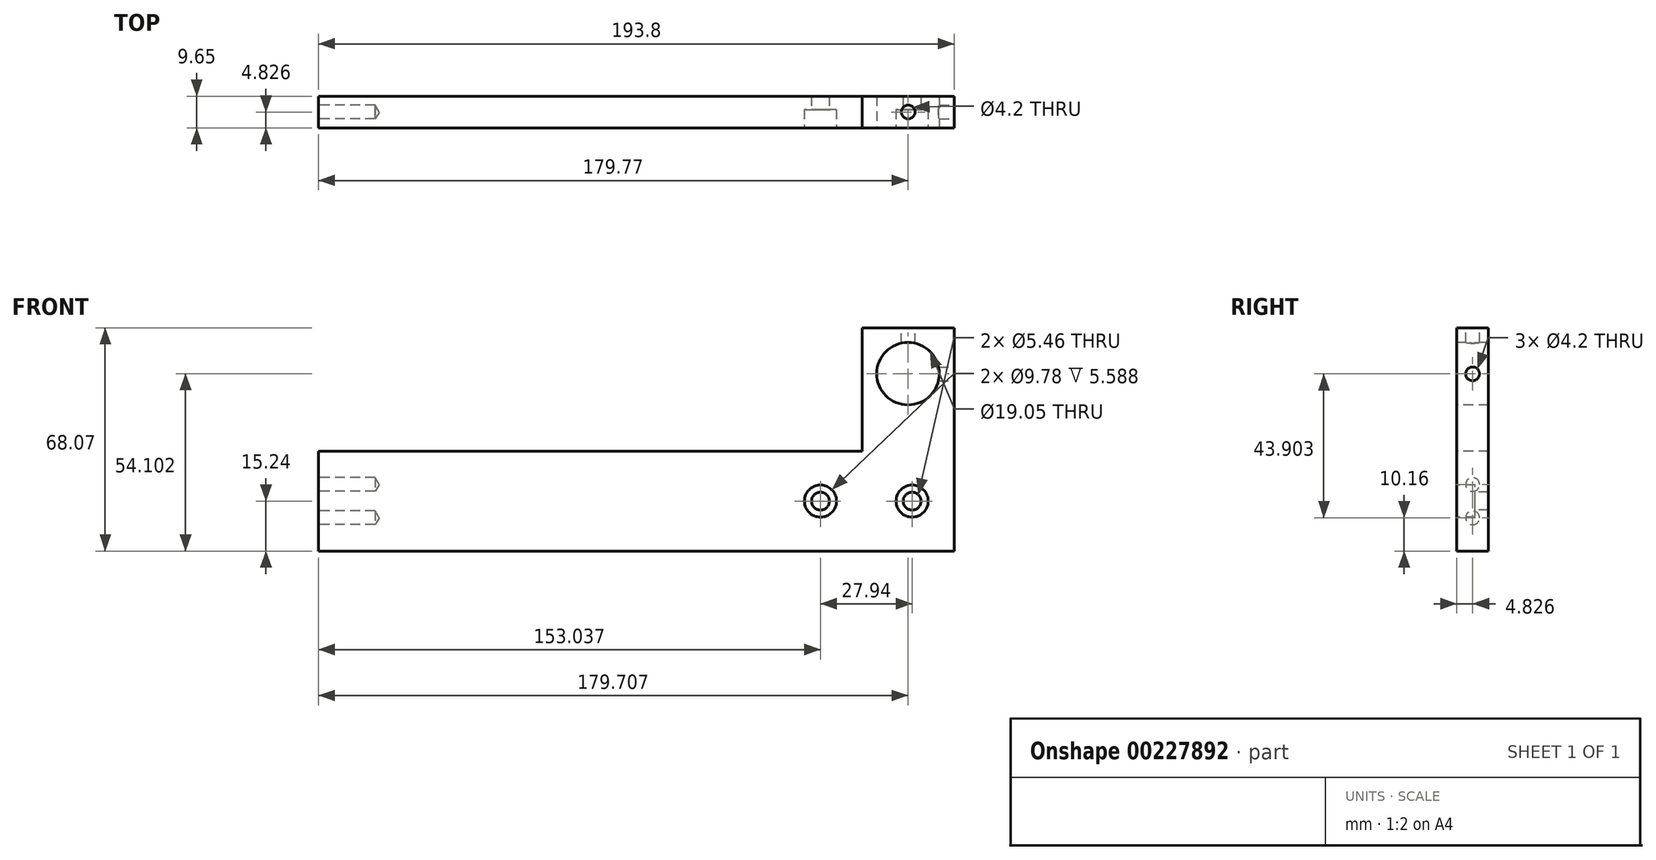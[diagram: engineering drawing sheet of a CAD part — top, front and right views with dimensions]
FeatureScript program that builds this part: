
annotation { "Feature Type Name" : "Feature", "Feature Type Description" : "" }
export const myFeature = defineFeature(function(context is Context, id is Id, definition is map)
    precondition{}
    {
        {
            var Q0;
            Q0=qCreatedBy(makeId("Front.planeOp"),FACE);
            var sketch = newSketch(context, id + "F0", { "sketchPlane" : qUnion([Q0])});
            skLineSegment(sketch, "E0", {"start": v(-79.83, 0) * mm, "end": v(113.97, 0) * mm});
            skLineSegment(sketch, "E1", {"start": v(-79.83, 0) * mm, "end": v(-79.83, 30.48) * mm});
            skLineSegment(sketch, "E2", {"start": v(-79.83, 30.48) * mm, "end": v(85.9, 30.48) * mm});
            skLineSegment(sketch, "E3", {"start": v(113.97, 0) * mm, "end": v(113.97, 68.07) * mm});
            skLineSegment(sketch, "E4", {"start": v(113.97, 68.07) * mm, "end": v(85.9, 68.07) * mm});
            skLineSegment(sketch, "E5", {"start": v(85.9, 68.07) * mm, "end": v(85.9, 30.48) * mm});
            skSolve(sketch);
        }
        {
            var Q0;
            Q0 = qSketchRegion(id + "F0", true);
            extrude(context, id + "F1", {"entities" : qUnion([Q0]), "oppositeDirection" : true, "depth" : 9.65 * mm});
        }
        {
            var Q0;
            Q0=makeQuery(id+"F1.opExtrude","CAP_FACE",FACE,{"disambiguationData":[OSD([sQuery(id+"F0.wireOp",EDGE,"E0"),sQuery(id+"F0.wireOp",EDGE,"E1"),sQuery(id+"F0.wireOp",EDGE,"E2"),sQuery(id+"F0.wireOp",EDGE,"E3"),sQuery(id+"F0.wireOp",EDGE,"E4"),sQuery(id+"F0.wireOp",EDGE,"E5")])],"isStart":true});
            var sketch = newSketch(context, id + "F2", { "sketchPlane" : qUnion([Q0])});
            skPoint(sketch, "E6", {"position": v(73.2, 15.24) * mm});
            skPoint(sketch, "E7", {"position": v(101.15, 15.24) * mm});
            skSolve(sketch);
        }
        {
            var Q0;
            Q0=sQuery(id+"F2.wireOp",VERTEX,"E6");
            var Q1;
            Q1=sQuery(id+"F2.wireOp",VERTEX,"E7");
            var Q2;
            Q2=makeQuery(id+"F1.opExtrude","SWEPT_BODY",BODY,{"disambiguationData":[OSD([sQuery(id+"F0.wireOp",EDGE,"E0"),sQuery(id+"F0.wireOp",EDGE,"E1"),sQuery(id+"F0.wireOp",EDGE,"E2"),sQuery(id+"F0.wireOp",EDGE,"E3"),sQuery(id+"F0.wireOp",EDGE,"E4"),sQuery(id+"F0.wireOp",EDGE,"E5")])]});
            hole(context, id + "F3", {"style" : HoleStyle.C_BORE, "endStyle" : HoleEndStyle.THROUGH, "holeDiameter" : 5.46 * mm, "cBoreDiameter" : 9.78 * mm, "cBoreDepth" : 5.6 * mm, "locations" : qUnion([Q0, Q1]), "scope" : qUnion([Q2]), "isTappedThrough" : true});
        }
        {
            var Q0;
            Q0=makeQuery(id+"F1.opExtrude","CAP_FACE",FACE,{"disambiguationData":[OSD([sQuery(id+"F0.wireOp",EDGE,"E0"),sQuery(id+"F0.wireOp",EDGE,"E1"),sQuery(id+"F0.wireOp",EDGE,"E2"),sQuery(id+"F0.wireOp",EDGE,"E3"),sQuery(id+"F0.wireOp",EDGE,"E4"),sQuery(id+"F0.wireOp",EDGE,"E5")])],"isStart":true});
            var sketch = newSketch(context, id + "F4", { "sketchPlane" : qUnion([Q0])});
            skPoint(sketch, "E8", {"position": v(99.88, 54.1) * mm});
            skSolve(sketch);
        }
        {
            var Q0;
            Q0=sQuery(id+"F4.wireOp",VERTEX,"E8");
            var Q1;
            Q1=makeQuery(id+"F1.opExtrude","SWEPT_BODY",BODY,{"disambiguationData":[OSD([sQuery(id+"F0.wireOp",EDGE,"E0"),sQuery(id+"F0.wireOp",EDGE,"E1"),sQuery(id+"F0.wireOp",EDGE,"E2"),sQuery(id+"F0.wireOp",EDGE,"E3"),sQuery(id+"F0.wireOp",EDGE,"E4"),sQuery(id+"F0.wireOp",EDGE,"E5")])]});
            hole(context, id + "F5", {"style" : HoleStyle.SIMPLE, "endStyle" : HoleEndStyle.THROUGH, "holeDiameter" : 19.05 * mm, "locations" : qUnion([Q0]), "scope" : qUnion([Q1]), "isTappedThrough" : true});
        }
        {
            var Q0;
            Q0=makeQuery(id+"F1.opExtrude","SWEPT_FACE",FACE,{"disambiguationData":[OSD([sQuery(id+"F0.wireOp",EDGE,"E4")])]});
            var sketch = newSketch(context, id + "F6", { "sketchPlane" : qUnion([Q0])});
            skPoint(sketch, "E9", {"position": v(99.94, 4.83) * mm});
            skSolve(sketch);
        }
        {
            var Q0;
            Q0=sQuery(id+"F6.wireOp",VERTEX,"E9");
            var Q1;
            Q1=makeQuery(id+"F1.opExtrude","SWEPT_BODY",BODY,{"disambiguationData":[OSD([sQuery(id+"F0.wireOp",EDGE,"E0"),sQuery(id+"F0.wireOp",EDGE,"E1"),sQuery(id+"F0.wireOp",EDGE,"E2"),sQuery(id+"F0.wireOp",EDGE,"E3"),sQuery(id+"F0.wireOp",EDGE,"E4"),sQuery(id+"F0.wireOp",EDGE,"E5")])]});
            hole(context, id + "F7", {"style" : HoleStyle.SIMPLE, "endStyle" : HoleEndStyle.BLIND, "standardTappedOrClearance" : lookupTablePath({ "standard" : "ISO", "engagement" : "75%", "pitch" : "0.8 mm", "size" : "M5", "type" : "Tapped" }), "standardBlindInLast" : lookupTablePath({ "standard" : "ISO", "engagement" : "75%", "pitch" : "0.8 mm", "size" : "M5", "type" : "Tapped" }), "holeDiameter" : 4.2 * mm, "holeDepth" : 12.7 * mm, "locations" : qUnion([Q0]), "scope" : qUnion([Q1]), "majorDiameter" : 5 * mm});
        }
        {
            var Q0;
            Q0=makeQuery(id+"F1.opExtrude","SWEPT_FACE",FACE,{"disambiguationData":[OSD([sQuery(id+"F0.wireOp",EDGE,"E3")])]});
            var sketch = newSketch(context, id + "F8", { "sketchPlane" : qUnion([Q0])});
            skPoint(sketch, "E10", {"position": v(4.83, 54.06) * mm});
            skPoint(sketch, "E11", {"position": v(0, 54.06) * mm});
            skSolve(sketch);
        }
        {
            var Q0;
            Q0=sQuery(id+"F8.wireOp",VERTEX,"E10");
            var Q1;
            Q1=makeQuery(id+"F1.opExtrude","SWEPT_BODY",BODY,{"disambiguationData":[OSD([sQuery(id+"F0.wireOp",EDGE,"E0"),sQuery(id+"F0.wireOp",EDGE,"E1"),sQuery(id+"F0.wireOp",EDGE,"E2"),sQuery(id+"F0.wireOp",EDGE,"E3"),sQuery(id+"F0.wireOp",EDGE,"E4"),sQuery(id+"F0.wireOp",EDGE,"E5")])]});
            hole(context, id + "F9", {"style" : HoleStyle.SIMPLE, "endStyle" : HoleEndStyle.BLIND, "standardTappedOrClearance" : lookupTablePath({ "standard" : "ISO", "engagement" : "75%", "pitch" : "0.8 mm", "size" : "M5", "type" : "Tapped" }), "standardBlindInLast" : lookupTablePath({ "standard" : "ISO", "engagement" : "75%", "pitch" : "0.8 mm", "size" : "M5", "type" : "Tapped" }), "holeDiameter" : 4.2 * mm, "holeDepth" : 12.7 * mm, "locations" : qUnion([Q0]), "scope" : qUnion([Q1]), "majorDiameter" : 5 * mm});
        }
        {
            var Q0;
            Q0=makeQuery(id+"F1.opExtrude","SWEPT_FACE",FACE,{"disambiguationData":[OSD([sQuery(id+"F0.wireOp",EDGE,"E1")])]});
            var sketch = newSketch(context, id + "F10", { "sketchPlane" : qUnion([Q0])});
            skPoint(sketch, "E12", {"position": v(-4.83, 64.78) * mm});
            skPoint(sketch, "E13", {"position": v(-4.83, 10.16) * mm});
            skPoint(sketch, "E14", {"position": v(-4.83, 20.32) * mm});
            skSolve(sketch);
        }
        {
            var Q0;
            Q0=sQuery(id+"F10.wireOp",VERTEX,"E14");
            var Q1;
            Q1=sQuery(id+"F10.wireOp",VERTEX,"E13");
            var Q2;
            Q2=makeQuery(id+"F1.opExtrude","SWEPT_BODY",BODY,{"disambiguationData":[OSD([sQuery(id+"F0.wireOp",EDGE,"E0"),sQuery(id+"F0.wireOp",EDGE,"E1"),sQuery(id+"F0.wireOp",EDGE,"E2"),sQuery(id+"F0.wireOp",EDGE,"E3"),sQuery(id+"F0.wireOp",EDGE,"E4"),sQuery(id+"F0.wireOp",EDGE,"E5")])]});
            hole(context, id + "F11", {"style" : HoleStyle.SIMPLE, "endStyle" : HoleEndStyle.BLIND, "standardTappedOrClearance" : lookupTablePath({ "standard" : "ISO", "engagement" : "75%", "pitch" : "0.8 mm", "size" : "M5", "type" : "Tapped" }), "standardBlindInLast" : lookupTablePath({ "standard" : "ISO", "engagement" : "75%", "pitch" : "0.8 mm", "size" : "M5", "type" : "Tapped" }), "holeDiameter" : 4.2 * mm, "holeDepth" : 17.27 * mm, "locations" : qUnion([Q0, Q1]), "scope" : qUnion([Q2]), "majorDiameter" : 5 * mm});
        }
        {
            var Q0;
            Q0=makeQuery(id+"F1.opExtrude","SWEPT_BODY",BODY,{"disambiguationData":[OSD([sQuery(id+"F0.wireOp",EDGE,"E0"),sQuery(id+"F0.wireOp",EDGE,"E1"),sQuery(id+"F0.wireOp",EDGE,"E2"),sQuery(id+"F0.wireOp",EDGE,"E3"),sQuery(id+"F0.wireOp",EDGE,"E4"),sQuery(id+"F0.wireOp",EDGE,"E5")])]});
            transform(context, id + "F12", {"entities" : qUnion([Q0]), "transformType" : TransformType.TRANSLATION_3D, "dx" : 0 * mm, "dy" : 0 * mm, "dz" : 0 * mm, "makeCopy" : true});
        }
        {
            var Q0;
            Q0=makeQuery(id+"F12.opPattern","COPY",BODY,{"derivedFrom":makeQuery(id+"F1.opExtrude","SWEPT_BODY",BODY,{"disambiguationData":[OSD([sQuery(id+"F0.wireOp",EDGE,"E0"),sQuery(id+"F0.wireOp",EDGE,"E1"),sQuery(id+"F0.wireOp",EDGE,"E2"),sQuery(id+"F0.wireOp",EDGE,"E3"),sQuery(id+"F0.wireOp",EDGE,"E4"),sQuery(id+"F0.wireOp",EDGE,"E5")])]}),"instanceName":"1"});
            deleteBodies(context, id + "F13", {"entities" : qUnion([Q0])});
        }
    });
